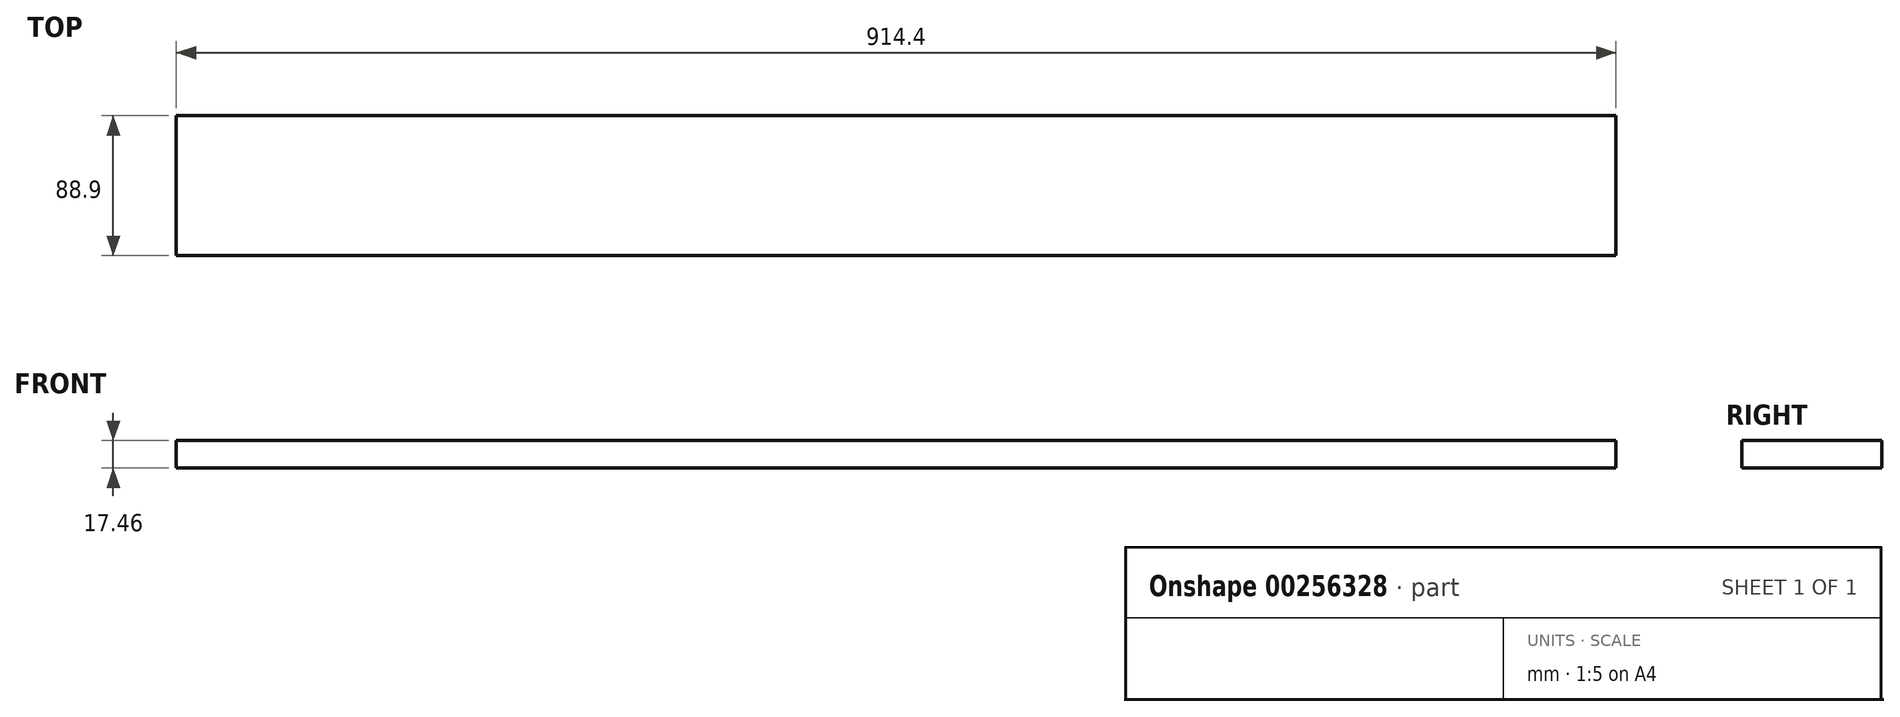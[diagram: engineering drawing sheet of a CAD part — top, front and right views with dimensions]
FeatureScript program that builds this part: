
annotation { "Feature Type Name" : "Feature", "Feature Type Description" : "" }
export const myFeature = defineFeature(function(context is Context, id is Id, definition is map)
    precondition{}
    {
        {
            var Q0;
            Q0=qCreatedBy(makeId("Right.planeOp"),FACE);
            var sketch = newSketch(context, id + "F0", { "sketchPlane" : qUnion([Q0])});
            skLineSegment(sketch, "E0.bottom", {"start": v(-44.45, 8.73) * mm, "end": v(44.45, 8.73) * mm});
            skLineSegment(sketch, "E0.top", {"start": v(-44.45, -8.73) * mm, "end": v(44.45, -8.73) * mm});
            skLineSegment(sketch, "E0.left", {"start": v(-44.45, 8.73) * mm, "end": v(-44.45, -8.73) * mm});
            skLineSegment(sketch, "E0.right", {"start": v(44.45, 8.73) * mm, "end": v(44.45, -8.73) * mm});
            skSolve(sketch);
        }
        {
            var Q0;
            Q0=qSketchRegion(id+"F0",true);
            extrude(context, id + "F1", {"entities" : qUnion([Q0]), "endBound" : BoundingType.SYMMETRIC, "depth" : 914.4 * mm});
        }
    });
